# Revit family: PRD_AR_MxrTps_WallFlange_ACXM1002 2
name_source: partatom
category: Plumbing Fixtures
units: mm (PartAtom-declared; Revit-internal decimal feet)

## family parameters
Cut with Voids When Loaded = No
Enable Cutting in Views = No
Host = Face
Maintain Annotation Orientation = No
OmniClass Number = 23.45.55.11
OmniClass Title = Sanitary Components
Part Type = Normal
Room Calculation Point = No
Round Connector Dimension = Use Diameter
Shared = No

## types (1)
- ACXM1002
    AssetType = Fixed
    BIMObjectName = PRD_AR_MixerTaps_WallFlange_ACXM1002
    BodyMaterial = PRD_AR_ChromatedBrass_HighPolished
    Category = PR_40_20_87_55, Mixer taps
    Default Elevation = 1050 mm
    Description = Wall flange for washbasin mixers with water connections positioned above one another. All-metal construction, high-polished chrome-plated brass, adjustable water connections.
    Export Type to IFC As = IfcDiscreteAccessoryType
    Features = All-metal construction, high-polished chrome-plated brass, adjustable water connections.
    Finish = high-polished
    IfcExportAs = IfcDiscreteAccessory
    IfcExportType = BRACKET
    IsExternal = No
    IsInsulated = No
    Manufacturer = KWC Group Management AG
    ManufacturerName = KWC Group Management AG
    ManufacturerURL = www.kwc-professional.com
    Material = chrome-plated brass
    Model = ACXM1002
    ModelNumber = 2030058762
    ModelReference = ACXM1002
    NBSDescription = Taps and water supply fittings for wash basins and troughs
    NBSReference = 45-35-70/345
    Name = Wall flange ACXM1002
    NominalDepth = 60 mm  [stored 0.19685 ft]
    NominalHeight = 110 mm  [stored 0.360892 ft]
    NominalWidth = 70 mm  [stored 0.229659 ft]
    ProductInformation = http://pim.kwc.com
    Quantity = 1
    QuantityUOM = piece
    Status = New
    Type IFC Predefined Type = BRACKET
    URL = www.kwc-professional.com
    Uniclass2015Code = Pr_40_20_87_55
    Uniclass2015Title = Mixer taps
    Uniclass2015Version = Products v1.38
    Version = 1

note: [stored X ft] marks values corroborated as IEEE doubles in the binary element streams (Revit-internal decimal feet)

## geometry (parser evidence)
native form markers: Sweep x5
no freeform markers — native parametric forms only
